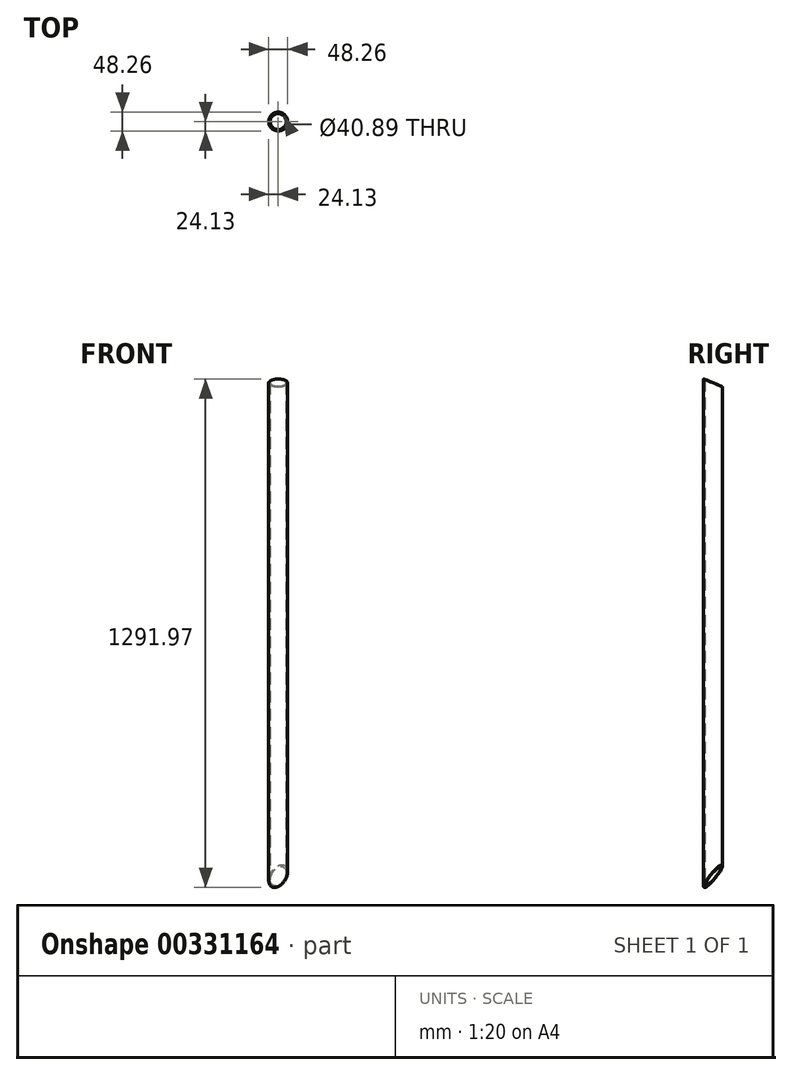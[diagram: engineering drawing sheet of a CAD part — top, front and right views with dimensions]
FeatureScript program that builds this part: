
annotation { "Feature Type Name" : "Feature", "Feature Type Description" : "" }
export const myFeature = defineFeature(function(context is Context, id is Id, definition is map)
    precondition{}
    {
        {
            var Q0;
            Q0=qCreatedBy(makeId("Top.planeOp"),FACE);
            var sketch = newSketch(context, id + "F0", { "sketchPlane" : qUnion([Q0])});
            skCircle(sketch, "E0", {"center": v(0, 0) * mm, "radius": 20.45 * mm});
            skCircle(sketch, "E1.0", {"center": v(0, 0) * mm, "radius": 24.13 * mm});
            skSolve(sketch);
        }
        {
            var Q0;
            Q0 = qSketchRegion(id + "F0", true);
            extrude(context, id + "F1", {"entities" : qUnion([Q0]), "depth" : 1308.1 * mm});
        }
        {
            var Q0;
            Q0=qCreatedBy(makeId("Right.planeOp"),FACE);
            var sketch = newSketch(context, id + "F2", { "sketchPlane" : qUnion([Q0])});
            skLineSegment(sketch, "E2.bottom", {"start": v(24.13, 1308.1) * mm, "end": v(-24.13, 1308.1) * mm});
            skLineSegment(sketch, "E2.left", {"start": v(24.13, 1308.1) * mm, "end": v(24.13, 1288.36) * mm});
            skPoint(sketch, "E2.middle", {"position": v(0, 1298.23) * mm});
            skLineSegment(sketch, "E3", {"start": v(-24.13, 1308.1) * mm, "end": v(24.13, 1288.36) * mm});
            skPoint(sketch, "E2.top.end.orphan", {"position": v(-24.13, 1288.36) * mm});
            skSolve(sketch);
        }
        {
            var Q0;
            Q0 = qSketchRegion(id + "F2", true);
            extrude(context, id + "F3", {"entities" : qUnion([Q0]), "operationType" : NewBodyOperationType.REMOVE, "endBound" : BoundingType.THROUGH_ALL, "oppositeDirection" : true, "depth" : 25.4 * mm, "hasSecondDirection" : true, "secondDirectionBound" : SecondDirectionBoundingType.THROUGH_ALL, "secondDirectionOppositeDirection" : false, "secondDirectionDepth" : 25.4 * mm});
        }
        {
            var Q0;
            Q0=qCreatedBy(makeId("Front.planeOp"),FACE);
            var sketch = newSketch(context, id + "F4", { "sketchPlane" : qUnion([Q0])});
            skLineSegment(sketch, "E4.top", {"start": v(28.58, 0) * mm, "end": v(-28.58, 0) * mm});
            skLineSegment(sketch, "E4.left", {"start": v(28.57, 26.65) * mm, "end": v(28.58, 0) * mm});
            skPoint(sketch, "E4.middle", {"position": v(0, 13.32) * mm});
            skLineSegment(sketch, "E5", {"start": v(-28.58, 0) * mm, "end": v(28.58, 26.65) * mm});
            skPoint(sketch, "E4.right.start.orphan", {"position": v(-28.58, 26.65) * mm});
            skSolve(sketch);
        }
        {
            var Q0;
            Q0 = qSketchRegion(id + "F4", true);
            extrude(context, id + "F5", {"entities" : qUnion([Q0]), "operationType" : NewBodyOperationType.REMOVE, "endBound" : BoundingType.THROUGH_ALL, "depth" : 25.4 * mm, "hasSecondDirection" : true, "secondDirectionBound" : SecondDirectionBoundingType.THROUGH_ALL, "secondDirectionOppositeDirection" : true, "secondDirectionDepth" : 25.4 * mm});
        }
        {
            var Q0;
            Q0=makeQuery(id+"F5.boolean.opBoolean","COPY",FACE,{"derivedFrom":makeQuery(id+"F5.opExtrude","SWEPT_FACE",FACE,{"disambiguationData":[OSD([sQuery(id+"F4.wireOp",EDGE,"E5")])]})});
            var sketch = newSketch(context, id + "F6", { "sketchPlane" : qUnion([Q0])});
            skLineSegment(sketch, "E6", {"start": v(-16.93, 0) * mm, "end": v(28.2, 0) * mm});
            skSolve(sketch);
        }
        {
            var Q0;
            Q0=sQuery(id+"F6.wireOp",EDGE,"E6");
            cPlane(context, id + "F7", {"entities" : qUnion([Q0]), "cplaneType" : CPlaneType.LINE_ANGLE, "offset" : 25.4 * mm, "angle" : 45 * degree, "oppositeDirection" : true, "width" : 152.4 * mm, "height" : 152.4 * mm});
        }
        {
            var Q0;
            Q0=qCreatedBy(id+"F7.planeOp",FACE);
            var sketch = newSketch(context, id + "F8", { "sketchPlane" : qUnion([Q0])});
            skLineSegment(sketch, "E7.bottom", {"start": v(-106, -71.8) * mm, "end": v(124.4, -71.8) * mm});
            skLineSegment(sketch, "E7.top", {"start": v(-106, 106.03) * mm, "end": v(124.4, 106.03) * mm});
            skLineSegment(sketch, "E7.left", {"start": v(-106, -71.8) * mm, "end": v(-106, 106.03) * mm});
            skLineSegment(sketch, "E7.right", {"start": v(124.4, -71.8) * mm, "end": v(124.4, 106.03) * mm});
            skPoint(sketch, "E7.middle", {"position": v(9.2, 17.12) * mm});
            skSolve(sketch);
        }
        {
            var Q0;
            Q0 = qSketchRegion(id + "F8", true);
            extrude(context, id + "F9", {"entities" : qUnion([Q0]), "operationType" : NewBodyOperationType.REMOVE, "depth" : 25.4 * mm, "hasSecondDirection" : true, "secondDirectionOppositeDirection" : true, "secondDirectionDepth" : 20.32 * mm});
        }
    });
